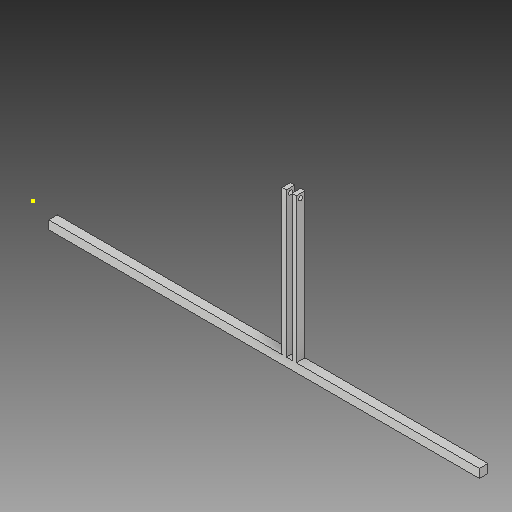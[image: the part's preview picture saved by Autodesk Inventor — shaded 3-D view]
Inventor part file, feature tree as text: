
AUTODESK INVENTOR PART (.ipt)
format: ipt  version: 2017 (Build 210142000, 142)  size: 132,608 bytes
history: native  units: in
note: dims shown in document units (in); Inventor stores cm internally (conversion verified against a paired STEP export)
features: thicken_offset x6, sketch x3, extrude x2, hole x1
ambient origin geometry x8: Origin, YZ Plane, XZ Plane, XY Plane, X Axis, Y Axis, Z Axis, Center Point
bodies: Solid1 (feature_tree)
feature tree (12):
  extrude  "Extrusion1"  Depth=0.25in
  extrude  "Extrusion3"  Depth=0.125in
  hole  "Hole2"  [1 undecoded]
  sketch  "Sketch4"  dims[d18=0.125in d19=4.191in d20=0.0in d21=0.125in d22=0.125in d23=0.125in d24=0.75in d25=0.375in d26=0.25in d27=0.5635in d28=1.0in d29=0.8108in d30=1.059in d31=1.059in d32=1.316in d33=1.316in d34=2.5in d35=2.5in d54=0.5in d55=0.5in d56=0.3in d57=0.3in d58=0.3in d59=0.3in]
  thicken_offset  "Thicken1"
  thicken_offset  "Thicken2"
  thicken_offset  "Thicken3"
  thicken_offset  "Thicken4"
  thicken_offset  "Thicken5"
  thicken_offset  "Thicken6"
  sketch  "Sketch1"  dims[d0=11.25in d1=0.25in]
  sketch  "Sketch3"  dims[d2=0.25in d3=0.0in d17=0.125in]
note: 1 required parameter value undecoded (feature->parameter linkage not recoverable at this tier; creation-order binding heuristic only, values carry confidence <= 0.55)
